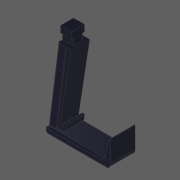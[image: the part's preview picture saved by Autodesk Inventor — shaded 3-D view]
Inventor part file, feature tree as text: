
AUTODESK INVENTOR PART (.ipt)
format: ipt  version: 2020 (Build 240168000, 168)  size: 271,872 bytes
history: native  units: in
note: dims shown in document units (in); Inventor stores cm internally (conversion verified against a paired STEP export)
features: fillet x5, other x3, extrude x3
ambient origin geometry x8: Origin, YZ Plane, XZ Plane, XY Plane, X Axis, Y Axis, Z Axis, Center Point
bodies: Solid1 (feature_tree)
feature tree (11):
  other  "Neck Start Plane"
  other  "Arm Profile"
  extrude  "Main Arm"  Depth=0.0039in
  extrude  "Pincher"  Depth=1.0386in
  extrude  "Neck"  Depth=0.7283in
  fillet  "Spring Hook Fillet"  Radius=0.1181in
  fillet  "Spring Attachment Fillet"  [1 undecoded]
  fillet  "Soft Edges"  Radius=0.195in
  fillet  "Pincher Fillet 1"  Radius=0.0197in
  fillet  "Pincher Fillet 2"  Radius=0.0394in
  other  "Neck Sketch"
note: 1 required parameter value undecoded (feature->parameter linkage not recoverable at this tier; creation-order binding heuristic only, values carry confidence <= 0.55)
